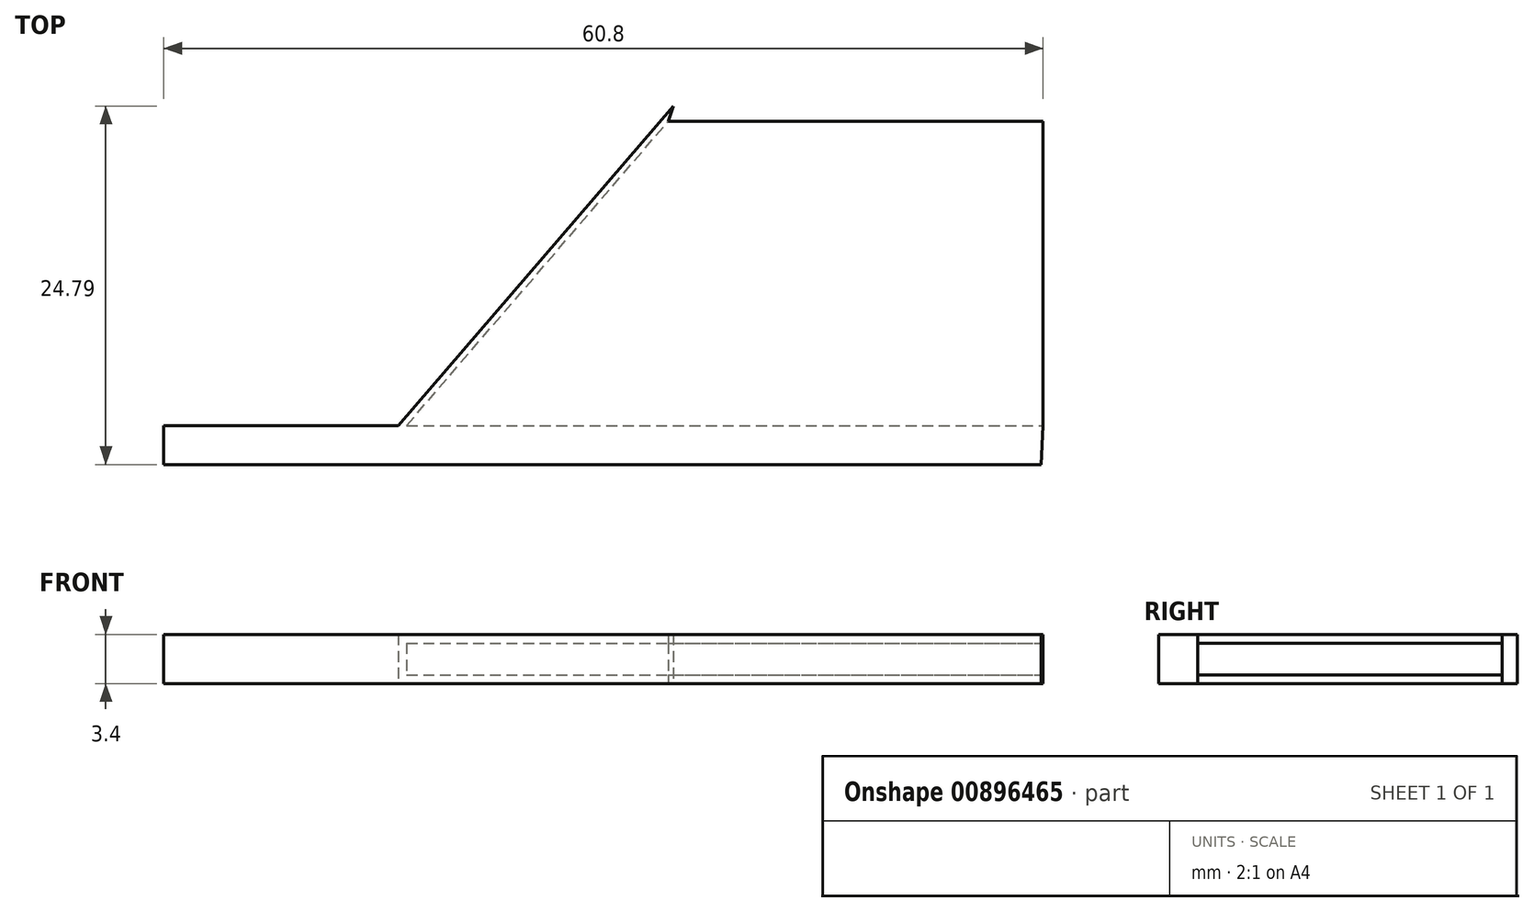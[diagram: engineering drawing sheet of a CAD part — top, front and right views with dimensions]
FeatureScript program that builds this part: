
annotation { "Feature Type Name" : "Feature", "Feature Type Description" : "" }
export const myFeature = defineFeature(function(context is Context, id is Id, definition is map)
    precondition{}
    {
        {
            var Q0;
            Q0=qCreatedBy(makeId("Top.planeOp"),FACE);
            var sketch = newSketch(context, id + "F0", { "sketchPlane" : qUnion([Q0])});
            skLineSegment(sketch, "E0", {"start": v(-12.67, 0) * mm, "end": v(48.13, 0) * mm});
            skLineSegment(sketch, "E1", {"start": v(48.13, 0) * mm, "end": v(48.13, 22.1) * mm});
            skLineSegment(sketch, "E2", {"start": v(48.13, 22.1) * mm, "end": v(22.55, 22.1) * mm});
            skLineSegment(sketch, "E3", {"start": v(22.55, 22.1) * mm, "end": v(3.55, 0) * mm});
            skLineSegment(sketch, "E4", {"start": v(-12.67, 0) * mm, "end": v(-12.67, -2.7) * mm});
            skLineSegment(sketch, "E5", {"start": v(-12.67, -2.7) * mm, "end": v(48, -2.7) * mm});
            skLineSegment(sketch, "E6", {"start": v(48, -2.7) * mm, "end": v(48.13, 0) * mm});
            skLineSegment(sketch, "E7", {"start": v(3.55, 0) * mm, "end": v(22.55, 22.1) * mm});
            skLineSegment(sketch, "E8", {"start": v(48.13, 22.1) * mm, "end": v(48.13, 0) * mm});
            skLineSegment(sketch, "E9", {"start": v(4.13, 0) * mm, "end": v(22.2, 21.03) * mm});
            skLineSegment(sketch, "E10", {"start": v(22.2, 21.03) * mm, "end": v(49.87, 21.03) * mm});
            skLineSegment(sketch, "E11", {"start": v(49.87, 21.03) * mm, "end": v(49.87, 0) * mm});
            skLineSegment(sketch, "E12", {"start": v(49.87, 21.03) * mm, "end": v(48.13, 22.1) * mm});
            skLineSegment(sketch, "E13", {"start": v(22.2, 21.03) * mm, "end": v(22.55, 22.1) * mm});
            skSolve(sketch);
        }
        {
            var Q0;
            Q0=makeQuery(id+"F0.imprint","IMPRINT",FACE,{"disambiguationData":[TD([[makeQuery(id+"F0.imprint","IMPRINT",EDGE,{"derivedFrom":sQuery(id+"F0.wireOp",EDGE,"E0")}),1.0]])]});
            var Q1;
            {var subQ3=sQuery(id+"F0.wireOp",EDGE,"E4");Q1=makeQuery(id+"F0.imprint","IMPRINT",FACE,{"disambiguationData":[TD([[makeQuery(id+"F0.imprint","IMPRINT",EDGE,{"derivedFrom":subQ3}),1.0]])]});}
            extrude(context, id + "F1", {"entities" : qUnion([Q0, Q1]), "depth" : 3.4 * mm, "offsetDistance" : 25 * mm});
        }
        {
            var Q0;
            {var subQ0=sQuery(id+"F0.wireOp",EDGE,"E9");Q0=makeQuery(id+"F0.imprint","IMPRINT",FACE,{"disambiguationData":[TD([[makeQuery(id+"F0.imprint","IMPRINT",EDGE,{"derivedFrom":subQ0}),-1.0]])]});}
            var Q1;
            {var subQ0=sQuery(id+"F0.wireOp",EDGE,"E2");Q1=makeQuery(id+"F0.imprint","IMPRINT",FACE,{"disambiguationData":[TD([[makeQuery(id+"F0.imprint","IMPRINT",EDGE,{"derivedFrom":subQ0}),1.0]])]});}
            extrude(context, id + "F2", {"entities" : qUnion([Q0, Q1]), "operationType" : NewBodyOperationType.REMOVE, "depth" : 2.8 * mm, "offsetDistance" : 25 * mm, "hasSecondDirection" : true, "secondDirectionOppositeDirection" : false, "secondDirectionDepth" : 0.6 * mm});
        }
    });
